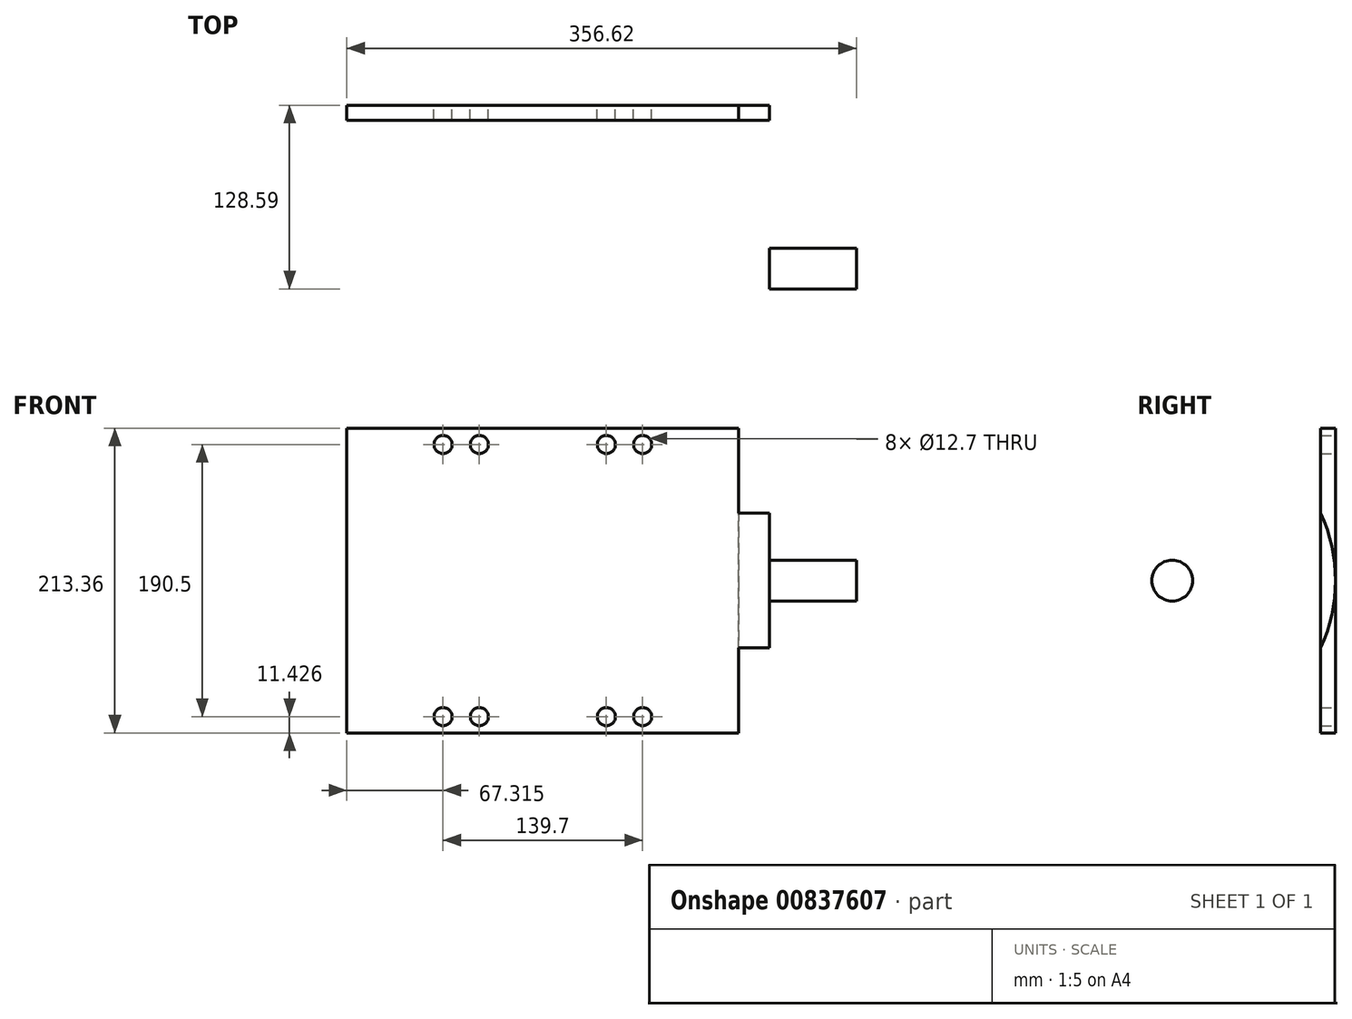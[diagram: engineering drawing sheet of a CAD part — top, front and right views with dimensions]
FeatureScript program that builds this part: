
annotation { "Feature Type Name" : "Feature", "Feature Type Description" : "" }
export const myFeature = defineFeature(function(context is Context, id is Id, definition is map)
    precondition{}
    {
        {
            var Q0;
            Q0=qCreatedBy(makeId("Front.planeOp"),FACE);
            var sketch = newSketch(context, id + "F0", { "sketchPlane" : qUnion([Q0])});
            skLineSegment(sketch, "E0.bottom", {"start": v(-218.32, 121.99) * mm, "end": v(56, 121.99) * mm});
            skLineSegment(sketch, "E0.top", {"start": v(-218.32, -91.37) * mm, "end": v(56, -91.37) * mm});
            skLineSegment(sketch, "E0.left", {"start": v(-218.32, 121.99) * mm, "end": v(-218.32, -91.37) * mm});
            skLineSegment(sketch, "E0.right", {"start": v(56, 121.99) * mm, "end": v(56, -91.37) * mm});
            skCircle(sketch, "E1", {"center": v(-151, 110.56) * mm, "radius": 6.35 * mm});
            skCircle(sketch, "E2", {"center": v(-151, -79.94) * mm, "radius": 6.35 * mm});
            skCircle(sketch, "E3", {"center": v(-36.7, 110.56) * mm, "radius": 6.35 * mm});
            skCircle(sketch, "E4", {"center": v(-36.7, -79.94) * mm, "radius": 6.35 * mm});
            skLineSegment(sketch, "E5", {"start": v(-151, 15.3) * mm, "end": v(-37.15, 15.3) * mm, "construction": true});
            skPoint(sketch, "E6", {"position": v(-218.32, 15.3) * mm});
            skCircle(sketch, "E7.1.0.0", {"center": v(-125.6, 110.56) * mm, "radius": 6.35 * mm});
            skCircle(sketch, "E7.1.0.1", {"center": v(-11.3, 110.56) * mm, "radius": 6.35 * mm});
            skCircle(sketch, "E7.1.0.2", {"center": v(-11.3, -79.94) * mm, "radius": 6.35 * mm});
            skCircle(sketch, "E7.1.0.3", {"center": v(-125.6, -79.94) * mm, "radius": 6.35 * mm});
            skLineSegment(sketch, "E8", {"start": v(-218.32, 15.3) * mm, "end": v(56, 15.3) * mm, "construction": true});
            skLineSegment(sketch, "E9", {"start": v(-81.16, 121.99) * mm, "end": v(-81.16, -91.37) * mm, "construction": true});
            skLineSegment(sketch, "E10", {"start": v(-81.16, 110.56) * mm, "end": v(-81.16, -79.94) * mm, "construction": true});
            skSolve(sketch);
        }
        {
            var Q0;
            Q0=makeQuery(id+"F0.imprint","IMPRINT",FACE,{"disambiguationData":[TD([[makeQuery(id+"F0.imprint","IMPRINT",EDGE,{"derivedFrom":sQuery(id+"F0.wireOp",EDGE,"E0.bottom")}),-1.0]])]});
            extrude(context, id + "F1", {"entities" : qUnion([Q0]), "depth" : 10.4 * mm, "offsetDistance" : 25.4 * mm});
        }
        {
            var Q0;
            Q0=makeQuery(id+"F1.opExtrude","SWEPT_FACE",FACE,{"disambiguationData":[OSD([sQuery(id+"F0.wireOp",EDGE,"E0.right")])]});
            var sketch = newSketch(context, id + "F2", { "sketchPlane" : qUnion([Q0])});
            skCircle(sketch, "E11", {"center": v(-111.89, 15.3) * mm, "radius": 111.89 * mm});
            skPoint(sketch, "E11.second.point", {"position": v(-222.72, 0) * mm});
            skPoint(sketch, "E11.third.point", {"position": v(-111.89, 127.2) * mm});
            skLineSegment(sketch, "E12", {"start": v(0, 121.99) * mm, "end": v(0, 15.3) * mm, "construction": true});
            skLineSegment(sketch, "E13", {"start": v(0, 15.3) * mm, "end": v(0, -91.37) * mm, "construction": true});
            skSolve(sketch);
        }
        {
            var Q0;
            {var subQ0=sQuery(id+"F2.wireOp",EDGE,"E11");var subQ1=makeQuery(id+"F1.opExtrude","CAP_EDGE",EDGE,{"disambiguationData":[OSD([sQuery(id+"F0.wireOp",EDGE,"E0.right")])],"isStart":false});var subQ2=makeQuery(id+"F2.imprint","INTERSECT",VERTEX,{"disambiguationData":[OD(0.0)],"derivedFrom":[subQ1,subQ0]});Q0=makeQuery(id+"F2.imprint","IMPRINT",FACE,{"disambiguationData":[TD([[makeQuery(id+"F2.imprint","IMPRINT",EDGE,{"disambiguationData":[TD([[subQ2,-1.0]])],"derivedFrom":subQ0}),1.0]])]});}
            extrude(context, id + "F3", {"entities" : qUnion([Q0]), "operationType" : NewBodyOperationType.ADD, "depth" : 21.59 * mm, "offsetDistance" : 25.4 * mm, "hasSecondDirection" : true, "secondDirectionOppositeDirection" : true, "secondDirectionDepth" : 274.32 * mm});
        }
        {
            var Q0;
            Q0=makeQuery(id+"F3.opExtrude","CAP_FACE",FACE,{"disambiguationData":[OSD([sQuery(id+"F0.wireOp",EDGE,"E0.right"),sQuery(id+"F2.wireOp",EDGE,"E11")])],"isStart":false});
            var sketch = newSketch(context, id + "F4", { "sketchPlane" : qUnion([Q0])});
            skLineSegment(sketch, "E14", {"start": v(0, 15.3) * mm, "end": v(-114.3, 15.3) * mm, "construction": true});
            skCircle(sketch, "E15", {"center": v(-114.3, 15.3) * mm, "radius": 14.29 * mm});
            skSolve(sketch);
        }
        {
            var Q0;
            Q0=makeQuery(id+"F4.imprint","IMPRINT",FACE,{"disambiguationData":[TD([[makeQuery(id+"F4.imprint","IMPRINT",EDGE,{"derivedFrom":sQuery(id+"F4.wireOp",EDGE,"E15")}),1.0]])]});
            extrude(context, id + "F5", {"entities" : qUnion([Q0]), "operationType" : NewBodyOperationType.ADD, "depth" : 60.7 * mm, "offsetDistance" : 25.4 * mm});
        }
    });
